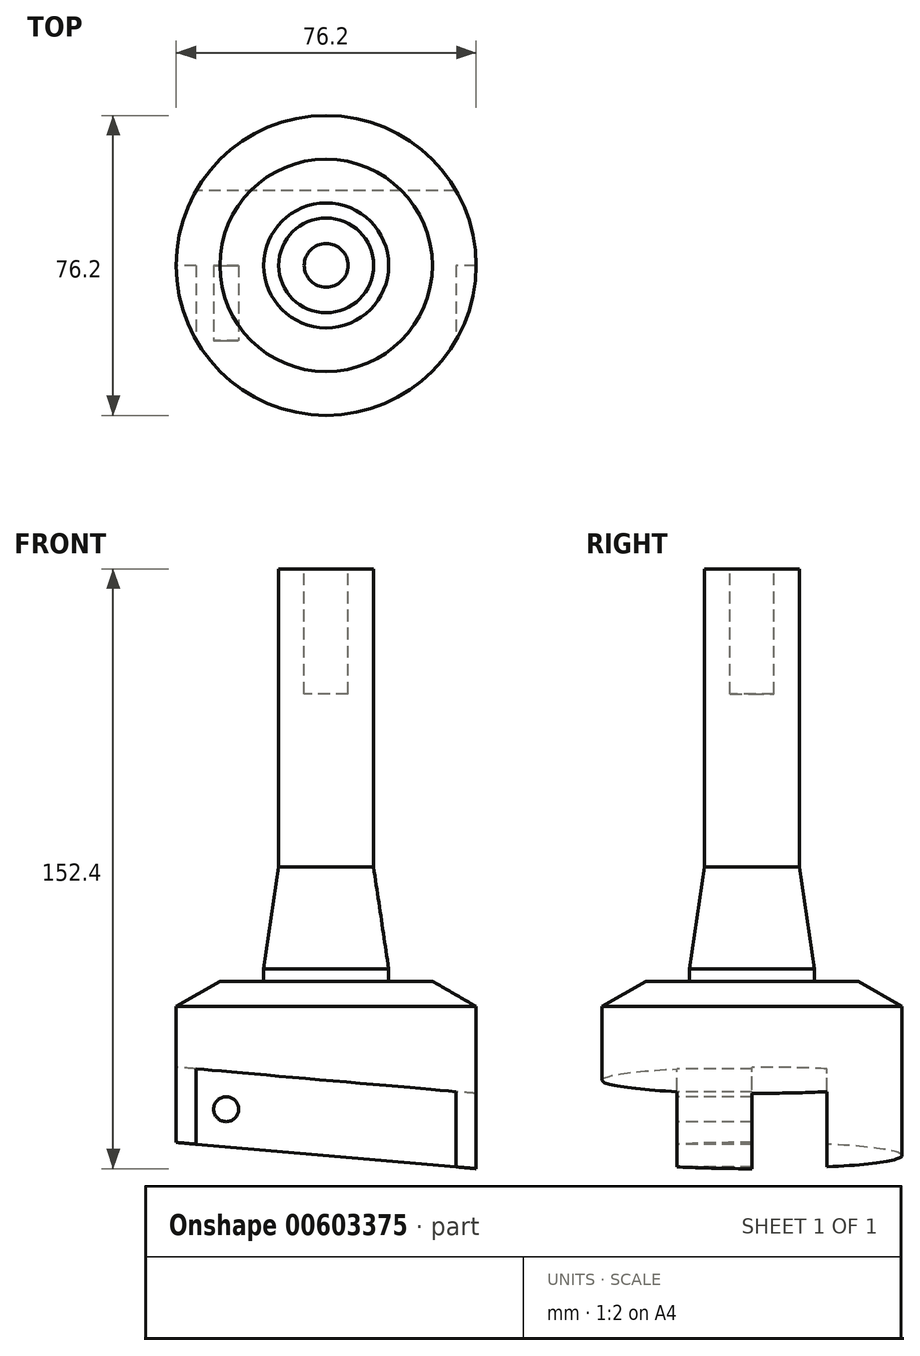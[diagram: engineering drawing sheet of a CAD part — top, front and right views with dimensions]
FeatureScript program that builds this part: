
annotation { "Feature Type Name" : "Feature", "Feature Type Description" : "" }
export const myFeature = defineFeature(function(context is Context, id is Id, definition is map)
    precondition{}
    {
        {
            var Q0;
            Q0=qCreatedBy(makeId("Front.planeOp"),FACE);
            var sketch = newSketch(context, id + "F0", { "sketchPlane" : qUnion([Q0])});
            skLineSegment(sketch, "E0.bottom", {"start": v(0, 50.8) * mm, "end": v(9.53, 50.8) * mm});
            skLineSegment(sketch, "E0.top", {"start": v(0, 0) * mm, "end": v(9.53, 0) * mm});
            skLineSegment(sketch, "E0.left", {"start": v(0, 50.8) * mm, "end": v(0, 0) * mm});
            skLineSegment(sketch, "E0.right", {"start": v(9.53, 50.8) * mm, "end": v(9.53, 0) * mm});
            skLineSegment(sketch, "E1.bottom", {"start": v(0, 0) * mm, "end": v(38.1, 0) * mm});
            skLineSegment(sketch, "E1.top", {"start": v(0, -50.8) * mm, "end": v(38.1, -50.8) * mm});
            skLineSegment(sketch, "E1.left", {"start": v(0, 0) * mm, "end": v(0, -50.8) * mm});
            skLineSegment(sketch, "E1.right", {"start": v(38.1, 0) * mm, "end": v(38.1, -50.8) * mm});
            skLineSegment(sketch, "E2", {"start": v(38.1, -50.8) * mm, "end": v(-38.1, -37.36) * mm});
            skLineSegment(sketch, "E3", {"start": v(0, -50.8) * mm, "end": v(-38.1, -50.8) * mm});
            skLineSegment(sketch, "E4", {"start": v(-38.1, -50.8) * mm, "end": v(-38.1, -18.02) * mm});
            skLineSegment(sketch, "E5", {"start": v(-38.1, -37.36) * mm, "end": v(-34.8, -18.6) * mm});
            skLineSegment(sketch, "E6", {"start": v(-34.8, -18.6) * mm, "end": v(38.1, -31.46) * mm});
            skLineSegment(sketch, "E7", {"start": v(-34.8, -18.6) * mm, "end": v(-38.1, -18.02) * mm});
            skLineSegment(sketch, "E8", {"start": v(0, 0) * mm, "end": v(0, 101.6) * mm});
            skPoint(sketch, "E8.endSnap0", {"position": v(0, 25.4) * mm});
            skLineSegment(sketch, "E9", {"start": v(0, 101.6) * mm, "end": v(12.05, 101.6) * mm});
            skLineSegment(sketch, "E10", {"start": v(0, 0) * mm, "end": v(15.88, 0) * mm});
            skLineSegment(sketch, "E11", {"start": v(15.88, 0) * mm, "end": v(12.05, 25.8) * mm});
            skLineSegment(sketch, "E12", {"start": v(12.05, 101.6) * mm, "end": v(12.05, 25.8) * mm});
            skLineSegment(sketch, "E13.bottom", {"start": v(15.88, 0) * mm, "end": v(38.1, 0) * mm});
            skLineSegment(sketch, "E13.top", {"start": v(15.88, -3.18) * mm, "end": v(38.1, -3.18) * mm});
            skLineSegment(sketch, "E13.left", {"start": v(15.88, 0) * mm, "end": v(15.88, -3.18) * mm});
            skLineSegment(sketch, "E13.right", {"start": v(38.1, 0) * mm, "end": v(38.1, -3.18) * mm});
            skLineSegment(sketch, "E14", {"start": v(38.1, -50.8) * mm, "end": v(-38.1, -44.13) * mm});
            skLineSegment(sketch, "E15", {"start": v(-38.1, -44.13) * mm, "end": v(-36.44, -25.16) * mm});
            skLineSegment(sketch, "E16", {"start": v(38.1, -31.68) * mm, "end": v(-36.44, -25.16) * mm});
            skLineSegment(sketch, "E17", {"start": v(-36.44, -25.16) * mm, "end": v(-38.1, -25.01) * mm});
            skLineSegment(sketch, "E18", {"start": v(26.99, -3.17) * mm, "end": v(38.1, -9.6) * mm});
            skSolve(sketch);
        }
        {
            var Q0;
            {var subQ0=sQuery(id+"F0.wireOp",EDGE,"E0.bottom");Q0=makeQuery(id+"F0.imprint","IMPRINT",FACE,{"disambiguationData":[TD([[makeQuery(id+"F0.imprint","IMPRINT",EDGE,{"derivedFrom":subQ0}),-1.0]])]});}
            var Q1;
            {var subQ2=sQuery(id+"F0.wireOp",EDGE,"E0.bottom");Q1=makeQuery(id+"F0.imprint","IMPRINT",FACE,{"disambiguationData":[TD([[makeQuery(id+"F0.imprint","IMPRINT",EDGE,{"derivedFrom":subQ2}),1.0]])]});}
            var Q2;
            {var subQ0=sQuery(id+"F0.wireOp",EDGE,"E6");var subQ1=sQuery(id+"F0.wireOp",EDGE,"E1.left");var subQ2=makeQuery(id+"F0.imprint","INTERSECT",VERTEX,{"derivedFrom":[subQ1,subQ0]});Q2=makeQuery(id+"F0.imprint","IMPRINT",FACE,{"disambiguationData":[TD([[makeQuery(id+"F0.imprint","IMPRINT",EDGE,{"disambiguationData":[TD([[subQ2,-1.0]])],"derivedFrom":subQ1}),1.0]])]});}
            var Q3;
            {var subQ0=sQuery(id+"F0.wireOp",EDGE,"E16");var subQ1=sQuery(id+"F0.wireOp",EDGE,"E1.left");var subQ2=makeQuery(id+"F0.imprint","INTERSECT",VERTEX,{"derivedFrom":[subQ1,subQ0]});Q3=makeQuery(id+"F0.imprint","IMPRINT",FACE,{"disambiguationData":[TD([[makeQuery(id+"F0.imprint","IMPRINT",EDGE,{"disambiguationData":[TD([[subQ2,-1.0]])],"derivedFrom":subQ1}),1.0]])]});}
            var Q4;
            {var subQ0=sQuery(id+"F0.wireOp",EDGE,"E2");var subQ1=sQuery(id+"F0.wireOp",EDGE,"E1.left");var subQ2=makeQuery(id+"F0.imprint","INTERSECT",VERTEX,{"derivedFrom":[subQ1,subQ0]});Q4=makeQuery(id+"F0.imprint","IMPRINT",FACE,{"disambiguationData":[TD([[makeQuery(id+"F0.imprint","IMPRINT",EDGE,{"disambiguationData":[TD([[subQ2,-1.0]])],"derivedFrom":subQ1}),1.0]])]});}
            var Q5;
            {var subQ0=sQuery(id+"F0.wireOp",EDGE,"E1.top");Q5=makeQuery(id+"F0.imprint","IMPRINT",FACE,{"disambiguationData":[TD([[makeQuery(id+"F0.imprint","IMPRINT",EDGE,{"derivedFrom":subQ0}),1.0]])]});}
            var Q6;
            {var subQ9=sQuery(id+"F0.wireOp",EDGE,"E13.left");Q6=makeQuery(id+"F0.imprint","IMPRINT",FACE,{"disambiguationData":[TD([[makeQuery(id+"F0.imprint","IMPRINT",EDGE,{"derivedFrom":subQ9}),-1.0]])]});}
            var Q7;
            Q7=sQuery(id+"F0.wireOp",EDGE,"E1.left");
            revolve(context, id + "F1", {"entities" : qUnion([Q0, Q1, Q2, Q3, Q4, Q5, Q6]), "axis" : qUnion([Q7]), "revolveType" : RevolveType.FULL});
        }
        {
            var Q0;
            {var subQ0=sQuery(id+"F0.wireOp",EDGE,"E3");Q0=makeQuery(id+"F0.imprint","IMPRINT",FACE,{"disambiguationData":[TD([[makeQuery(id+"F0.imprint","IMPRINT",EDGE,{"derivedFrom":subQ0}),-1.0]])]});}
            var Q1;
            {var subQ0=sQuery(id+"F0.wireOp",EDGE,"E1.top");Q1=makeQuery(id+"F0.imprint","IMPRINT",FACE,{"disambiguationData":[TD([[makeQuery(id+"F0.imprint","IMPRINT",EDGE,{"derivedFrom":subQ0}),1.0]])]});}
            extrude(context, id + "F2", {"entities" : qUnion([Q0, Q1]), "operationType" : NewBodyOperationType.REMOVE, "endBound" : BoundingType.SYMMETRIC, "oppositeDirection" : true, "depth" : 76.2 * mm, "offsetDistance" : 25.4 * mm});
        }
        {
            var Q0;
            {var subQ0=sQuery(id+"F0.wireOp",EDGE,"E16");var subQ1=sQuery(id+"F0.wireOp",EDGE,"E1.left");var subQ2=makeQuery(id+"F0.imprint","INTERSECT",VERTEX,{"derivedFrom":[subQ1,subQ0]});Q0=makeQuery(id+"F0.imprint","IMPRINT",FACE,{"disambiguationData":[TD([[makeQuery(id+"F0.imprint","IMPRINT",EDGE,{"disambiguationData":[TD([[subQ2,-1.0]])],"derivedFrom":subQ1}),1.0]])]});}
            var Q1;
            {var subQ5=sQuery(id+"F0.wireOp",EDGE,"E1.left");var subQ7=sQuery(id+"F0.wireOp",EDGE,"E16");var subQ9=makeQuery(id+"F0.imprint","INTERSECT",VERTEX,{"derivedFrom":[subQ5,subQ7]});Q1=makeQuery(id+"F0.imprint","IMPRINT",FACE,{"disambiguationData":[TD([[makeQuery(id+"F0.imprint","IMPRINT",EDGE,{"disambiguationData":[TD([[subQ9,-1.0]])],"derivedFrom":subQ5}),-1.0]])]});}
            var Q2;
            {var subQ0=sQuery(id+"F0.wireOp",EDGE,"E2");var subQ1=sQuery(id+"F0.wireOp",EDGE,"E1.left");var subQ2=makeQuery(id+"F0.imprint","INTERSECT",VERTEX,{"derivedFrom":[subQ1,subQ0]});Q2=makeQuery(id+"F0.imprint","IMPRINT",FACE,{"disambiguationData":[TD([[makeQuery(id+"F0.imprint","IMPRINT",EDGE,{"disambiguationData":[TD([[subQ2,-1.0]])],"derivedFrom":subQ1}),-1.0]])]});}
            var Q3;
            {var subQ0=sQuery(id+"F0.wireOp",EDGE,"E2");var subQ1=sQuery(id+"F0.wireOp",EDGE,"E1.left");var subQ2=makeQuery(id+"F0.imprint","INTERSECT",VERTEX,{"derivedFrom":[subQ1,subQ0]});Q3=makeQuery(id+"F0.imprint","IMPRINT",FACE,{"disambiguationData":[TD([[makeQuery(id+"F0.imprint","IMPRINT",EDGE,{"disambiguationData":[TD([[subQ2,-1.0]])],"derivedFrom":subQ1}),1.0]])]});}
            var Q4;
            {var subQ0=sQuery(id+"F0.wireOp",EDGE,"E15");var subQ1=sQuery(id+"F0.wireOp",EDGE,"E5");var subQ2=makeQuery(id+"F0.imprint","INTERSECT",VERTEX,{"derivedFrom":[subQ1,subQ0]});Q4=makeQuery(id+"F0.imprint","IMPRINT",FACE,{"disambiguationData":[TD([[makeQuery(id+"F0.imprint","IMPRINT",EDGE,{"disambiguationData":[TD([[subQ2,-1.0]])],"derivedFrom":subQ1}),1.0]])]});}
            var Q5;
            {var subQ3=sQuery(id+"F0.wireOp",EDGE,"E17");Q5=makeQuery(id+"F0.imprint","IMPRINT",FACE,{"disambiguationData":[TD([[makeQuery(id+"F0.imprint","IMPRINT",EDGE,{"derivedFrom":subQ3}),1.0]])]});}
            var Q6;
            {var subQ1=sQuery(id+"F0.wireOp",EDGE,"E2");var subQ3=sQuery(id+"F0.wireOp",EDGE,"E15");var subQ4=makeQuery(id+"F0.imprint","INTERSECT",VERTEX,{"derivedFrom":[subQ1,subQ3]});Q6=makeQuery(id+"F0.imprint","IMPRINT",FACE,{"disambiguationData":[TD([[makeQuery(id+"F0.imprint","IMPRINT",EDGE,{"disambiguationData":[TD([[subQ4,-1.0]])],"derivedFrom":subQ3}),1.0]])]});}
            var Q7;
            {var subQ1=sQuery(id+"F0.wireOp",EDGE,"E2");var subQ3=sQuery(id+"F0.wireOp",EDGE,"E15");var subQ4=makeQuery(id+"F0.imprint","INTERSECT",VERTEX,{"derivedFrom":[subQ1,subQ3]});Q7=makeQuery(id+"F0.imprint","IMPRINT",FACE,{"disambiguationData":[TD([[makeQuery(id+"F0.imprint","IMPRINT",EDGE,{"disambiguationData":[TD([[subQ4,-1.0]])],"derivedFrom":subQ1}),1.0]])]});}
            extrude(context, id + "F3", {"entities" : qUnion([Q0, Q1, Q2, Q3, Q4, Q5, Q6, Q7]), "operationType" : NewBodyOperationType.REMOVE, "oppositeDirection" : true, "depth" : 19.05 * mm, "offsetDistance" : 25.4 * mm});
        }
        {
            var Q0;
            {var subQ0=sQuery(id+"F0.wireOp",EDGE,"E1.right");var subQ1=sQuery(id+"F0.wireOp",EDGE,"E14");Q0=makeQuery(id+"F3.boolean.opBoolean","SPLIT",FACE,{"disambiguationData":[TD([makeQuery(id+"F3.opExtrude","CAP_FACE",FACE,{"disambiguationData":[OSD([subQ0,sQuery(id+"F0.wireOp",EDGE,"E4"),subQ1,sQuery(id+"F0.wireOp",EDGE,"E16"),sQuery(id+"F0.wireOp",EDGE,"E17")])],"isStart":true})])],"derivedFrom":makeQuery(id+"F2.boolean.opBoolean","COPY",FACE,{"derivedFrom":makeQuery(id+"F2.opExtrude","SWEPT_FACE",FACE,{"disambiguationData":[OSD([subQ1])]})})});}
            var sketch = newSketch(context, id + "F4", { "sketchPlane" : qUnion([Q0])});
            skLineSegment(sketch, "E19", {"start": v(4.58, 19.05) * mm, "end": v(-34.1, 19.05) * mm});
            skLineSegment(sketch, "E20", {"start": v(-34.1, 19.05) * mm, "end": v(37.26, 19.05) * mm});
            skLineSegment(sketch, "E21", {"start": v(-34.1, 0) * mm, "end": v(-34.1, 19.05) * mm});
            skLineSegment(sketch, "E22", {"start": v(4.14, 38.1) * mm, "end": v(-34.1, 38.14) * mm});
            skLineSegment(sketch, "E23", {"start": v(-34.1, 38.14) * mm, "end": v(-34.1, 19.05) * mm});
            skSolve(sketch);
        }
        {
            var Q0;
            {var subQ8=sQuery(id+"F4.wireOp",EDGE,"E22");Q0=makeQuery(id+"F4.imprint","IMPRINT",FACE,{"disambiguationData":[TD([[makeQuery(id+"F4.imprint","IMPRINT",EDGE,{"derivedFrom":subQ8}),1.0]])]});}
            var Q1;
            {var subQ0=sQuery(id+"F4.wireOp",EDGE,"E20");var subQ1=makeQuery(id+"F4.imprint","IMPRINT",VERTEX,{"derivedFrom":subQ0});Q1=makeQuery(id+"F4.imprint","IMPRINT",FACE,{"disambiguationData":[TD([[makeQuery(id+"F4.imprint","IMPRINT",EDGE,{"disambiguationData":[TD([[subQ1,1.0]])],"derivedFrom":subQ0}),1.0]])]});}
            extrude(context, id + "F5", {"entities" : qUnion([Q0, Q1]), "operationType" : NewBodyOperationType.REMOVE, "oppositeDirection" : true, "depth" : 19.05 * mm, "offsetDistance" : 25.4 * mm});
        }
        {
            var Q0;
            Q0=makeQuery(id+"F5.boolean.opBoolean","COPY",FACE,{"derivedFrom":makeQuery(id+"F5.opExtrude","SWEPT_FACE",FACE,{"disambiguationData":[OSD([sQuery(id+"F4.wireOp",EDGE,"E20")])]})});
            var sketch = newSketch(context, id + "F6", { "sketchPlane" : qUnion([Q0])});
            skLineSegment(sketch, "E24", {"start": v(-33, -35.02) * mm, "end": v(33, -40.8) * mm});
            skCircle(sketch, "E25", {"center": v(0, -37.9) * mm, "radius": 3.18 * mm});
            skCircle(sketch, "E26", {"center": v(-25.4, -35.68) * mm, "radius": 3.18 * mm});
            skCircle(sketch, "E27", {"center": v(25.4, -40.13) * mm, "radius": 3.18 * mm});
            skSolve(sketch);
        }
        {
            var Q0;
            {var subQ0=sQuery(id+"F6.wireOp",EDGE,"E25");var subQ1=sQuery(id+"F6.wireOp",EDGE,"E24");var subQ2=makeQuery(id+"F6.imprint","INTERSECT",VERTEX,{"disambiguationData":[OD(0.0)],"derivedFrom":[subQ1,subQ0]});Q0=makeQuery(id+"F6.imprint","IMPRINT",FACE,{"disambiguationData":[TD([[makeQuery(id+"F6.imprint","IMPRINT",EDGE,{"disambiguationData":[TD([[subQ2,-1.0]])],"derivedFrom":subQ1}),-1.0]])]});}
            var Q1;
            {var subQ0=sQuery(id+"F6.wireOp",EDGE,"E25");var subQ1=sQuery(id+"F6.wireOp",EDGE,"E24");var subQ2=makeQuery(id+"F6.imprint","INTERSECT",VERTEX,{"disambiguationData":[OD(0.0)],"derivedFrom":[subQ1,subQ0]});Q1=makeQuery(id+"F6.imprint","IMPRINT",FACE,{"disambiguationData":[TD([[makeQuery(id+"F6.imprint","IMPRINT",EDGE,{"disambiguationData":[TD([[subQ2,-1.0]])],"derivedFrom":subQ1}),1.0]])]});}
            var Q2;
            {var subQ0=sQuery(id+"F6.wireOp",EDGE,"E26");var subQ1=sQuery(id+"F6.wireOp",EDGE,"E24");var subQ2=makeQuery(id+"F6.imprint","INTERSECT",VERTEX,{"disambiguationData":[OD(0.0)],"derivedFrom":[subQ1,subQ0]});Q2=makeQuery(id+"F6.imprint","IMPRINT",FACE,{"disambiguationData":[TD([[makeQuery(id+"F6.imprint","IMPRINT",EDGE,{"disambiguationData":[TD([[subQ2,-1.0]])],"derivedFrom":subQ1}),1.0]])]});}
            var Q3;
            {var subQ0=sQuery(id+"F6.wireOp",EDGE,"E26");var subQ1=sQuery(id+"F6.wireOp",EDGE,"E24");var subQ2=makeQuery(id+"F6.imprint","INTERSECT",VERTEX,{"disambiguationData":[OD(0.0)],"derivedFrom":[subQ1,subQ0]});Q3=makeQuery(id+"F6.imprint","IMPRINT",FACE,{"disambiguationData":[TD([[makeQuery(id+"F6.imprint","IMPRINT",EDGE,{"disambiguationData":[TD([[subQ2,-1.0]])],"derivedFrom":subQ1}),-1.0]])]});}
            var Q4;
            {var subQ0=sQuery(id+"F6.wireOp",EDGE,"E27");var subQ1=sQuery(id+"F6.wireOp",EDGE,"E24");var subQ2=makeQuery(id+"F6.imprint","INTERSECT",VERTEX,{"disambiguationData":[OD(0.0)],"derivedFrom":[subQ1,subQ0]});Q4=makeQuery(id+"F6.imprint","IMPRINT",FACE,{"disambiguationData":[TD([[makeQuery(id+"F6.imprint","IMPRINT",EDGE,{"disambiguationData":[TD([[subQ2,-1.0]])],"derivedFrom":subQ1}),-1.0]])]});}
            var Q5;
            {var subQ0=sQuery(id+"F6.wireOp",EDGE,"E27");var subQ1=sQuery(id+"F6.wireOp",EDGE,"E24");var subQ2=makeQuery(id+"F6.imprint","INTERSECT",VERTEX,{"disambiguationData":[OD(0.0)],"derivedFrom":[subQ1,subQ0]});Q5=makeQuery(id+"F6.imprint","IMPRINT",FACE,{"disambiguationData":[TD([[makeQuery(id+"F6.imprint","IMPRINT",EDGE,{"disambiguationData":[TD([[subQ2,-1.0]])],"derivedFrom":subQ1}),1.0]])]});}
            extrude(context, id + "F7", {"entities" : qUnion([Q0, Q1, Q2, Q3, Q4, Q5]), "operationType" : NewBodyOperationType.REMOVE, "oppositeDirection" : true, "depth" : 19.05 * mm, "offsetDistance" : 25.4 * mm});
        }
        {
            var Q0;
            Q0=makeQuery(id+"F1.opRevolve","SWEPT_FACE",FACE,{"disambiguationData":[OSD([sQuery(id+"F0.wireOp",EDGE,"E9")])]});
            var sketch = newSketch(context, id + "F8", { "sketchPlane" : qUnion([Q0])});
            skCircle(sketch, "E28", {"center": v(0, 0) * mm, "radius": 5.56 * mm});
            skSolve(sketch);
        }
        {
            var Q0;
            Q0=makeQuery(id+"F8.imprint","IMPRINT",FACE,{"disambiguationData":[TD([[makeQuery(id+"F8.imprint","IMPRINT",EDGE,{"derivedFrom":sQuery(id+"F8.wireOp",EDGE,"E28")}),1.0]])]});
            extrude(context, id + "F9", {"entities" : qUnion([Q0]), "operationType" : NewBodyOperationType.REMOVE, "oppositeDirection" : true, "depth" : 31.75 * mm, "offsetDistance" : 25.4 * mm});
        }
    });
